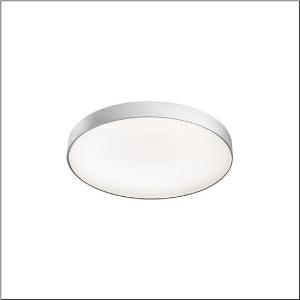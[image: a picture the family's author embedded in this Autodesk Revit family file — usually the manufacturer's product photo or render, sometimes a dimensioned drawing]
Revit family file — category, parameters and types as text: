
# Revit family: round_21_m_51mr36nd0321s
name_source: partatom
category: Lighting Fixtures
units: mm (PartAtom-declared; Revit-internal decimal feet)

## family parameters
Cut with Voids When Loaded = No
Host = Face
Light Source = No
Part Type = Normal
Room Calculation Point = No
Round Connector Dimension = Use Diameter
Shared = No

## types (1)
- Round 21 M (1 x LED, 7170 lm, 54.6 W, 3000K)
    Apparent Load = 55 VA
    CIE Flux Codes = 66 90 98 84 100
    Color Rendering = 80
    Color Temperature = 3000K
    Default Elevation = 1800 mm
    Description = Round 21 M, wall and ceiling luminaire, primary optical cover: micro prismatic cover, of PMMA, transparent, CAT 2 (L<= 3000cd/m²), light emission: direct/indirect distribution, primary light characteristic: symmetric, installation type: surface-mounted, suspended mounting, LED, rated luminous flux: 7.130lm, luminous efficacy: 131lm/W, light colour: 830, colour temperature: 3000K, control gear: DALI 2, with terminal, 5-pole, mains connection: 230V, AC, 50/60Hz, rated input power: 54.6W, housing, of aluminium, coated, silver, diameter: 600mm, height: 62mm, protection rating (complete): IP40, insulation class (complete): insulation class I (protective earthing), certification: CE, impact resistance: IK04, permissible operating ambient temperature: -10..+35°C, packaging unit: 1 piece
    Height = 87 mm
    Lamp = 1 x LED
    Lamp Light Flux = 7170 lm
    Lamp Power = 54.6 W
    Lamp count = 1
    Length = 600 mm
    Luminous efficacy = 131 lm/W
    Manufacturer = Siteco
    ModVariant = No
    Model = 51MR36ND0321S
    Mounting Place = Ceiling
    Mounting Type = Surface mounted
    Number of Poles = 1
    OnlyDefault = Yes
    Power Factor = 1
    Product Name = Round 21 M
    Product group = wall and ceiling luminaire | ceiling mounted
    ProductGroupID = 304
    Protection Class = Protection class I
    Protection Degree = IP 40
    RLX_Detail_Level = 1
    RLX_Emergency_Light_Flux = 0 lm
    RLX_Emergency_Type = 0
    RLX_Emergency_Type_DB = No
    RlxData = <blob elided: 19049 chars, md5=677c5330>
    Socket = socket
    Standby Power = 0 W
    System Light Flux = 7170 lm
    System Power = 55 W
    Type Comments = Product without accessories
    Type Image = l_1258301.jpg
    URL = http://relux.com
    VarID = ---
    Voltage = 0 V
    Weight = 0.00 kg
    Width = 0 mm  [stored 0 ft]

note: [stored X ft] marks values corroborated as IEEE doubles in the binary element streams (Revit-internal decimal feet)

## geometry (parser evidence)
native form markers: Blend x4, Sweep x14
no freeform markers — native parametric forms only
